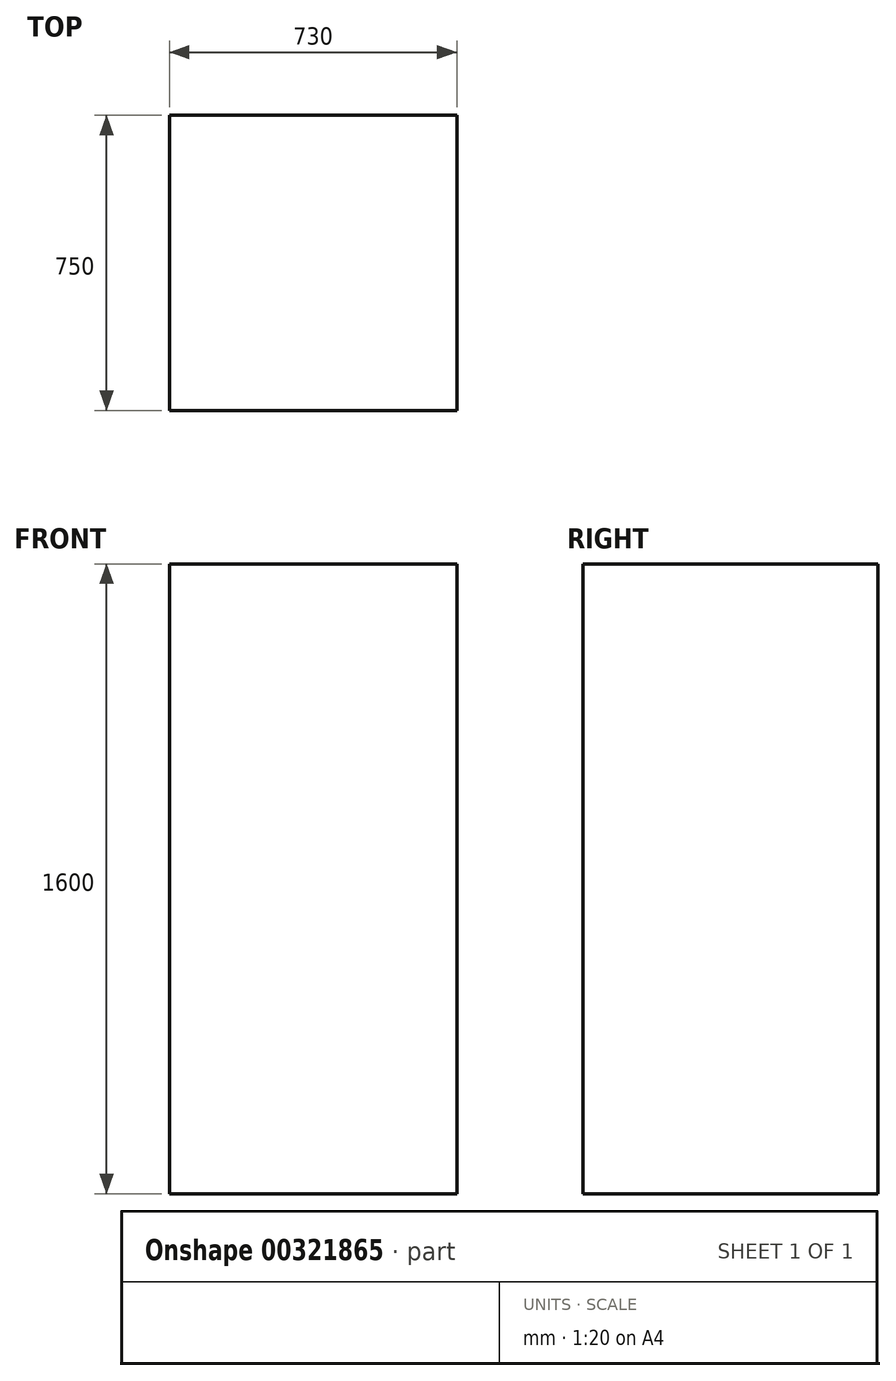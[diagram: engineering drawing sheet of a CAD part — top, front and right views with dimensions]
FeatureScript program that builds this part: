
annotation { "Feature Type Name" : "Feature", "Feature Type Description" : "" }
export const myFeature = defineFeature(function(context is Context, id is Id, definition is map)
    precondition{}
    {
        {
            var Q0;
            Q0=qCreatedBy(makeId("Top.planeOp"),FACE);
            var sketch = newSketch(context, id + "F0", { "sketchPlane" : qUnion([Q0])});
            skLineSegment(sketch, "E0.bottom", {"start": v(365, 375) * mm, "end": v(-365, 375) * mm});
            skLineSegment(sketch, "E0.top", {"start": v(365, -375) * mm, "end": v(-365, -375) * mm});
            skLineSegment(sketch, "E0.left", {"start": v(365, 375) * mm, "end": v(365, -375) * mm});
            skLineSegment(sketch, "E0.right", {"start": v(-365, 375) * mm, "end": v(-365, -375) * mm});
            skPoint(sketch, "E0.middle", {"position": v(0, 0) * mm});
            skSolve(sketch);
        }
        {
            var Q0;
            Q0 = qSketchRegion(id + "F0", true);
            extrude(context, id + "F1", {"entities" : qUnion([Q0]), "depth" : 1600 * mm});
        }
    });
